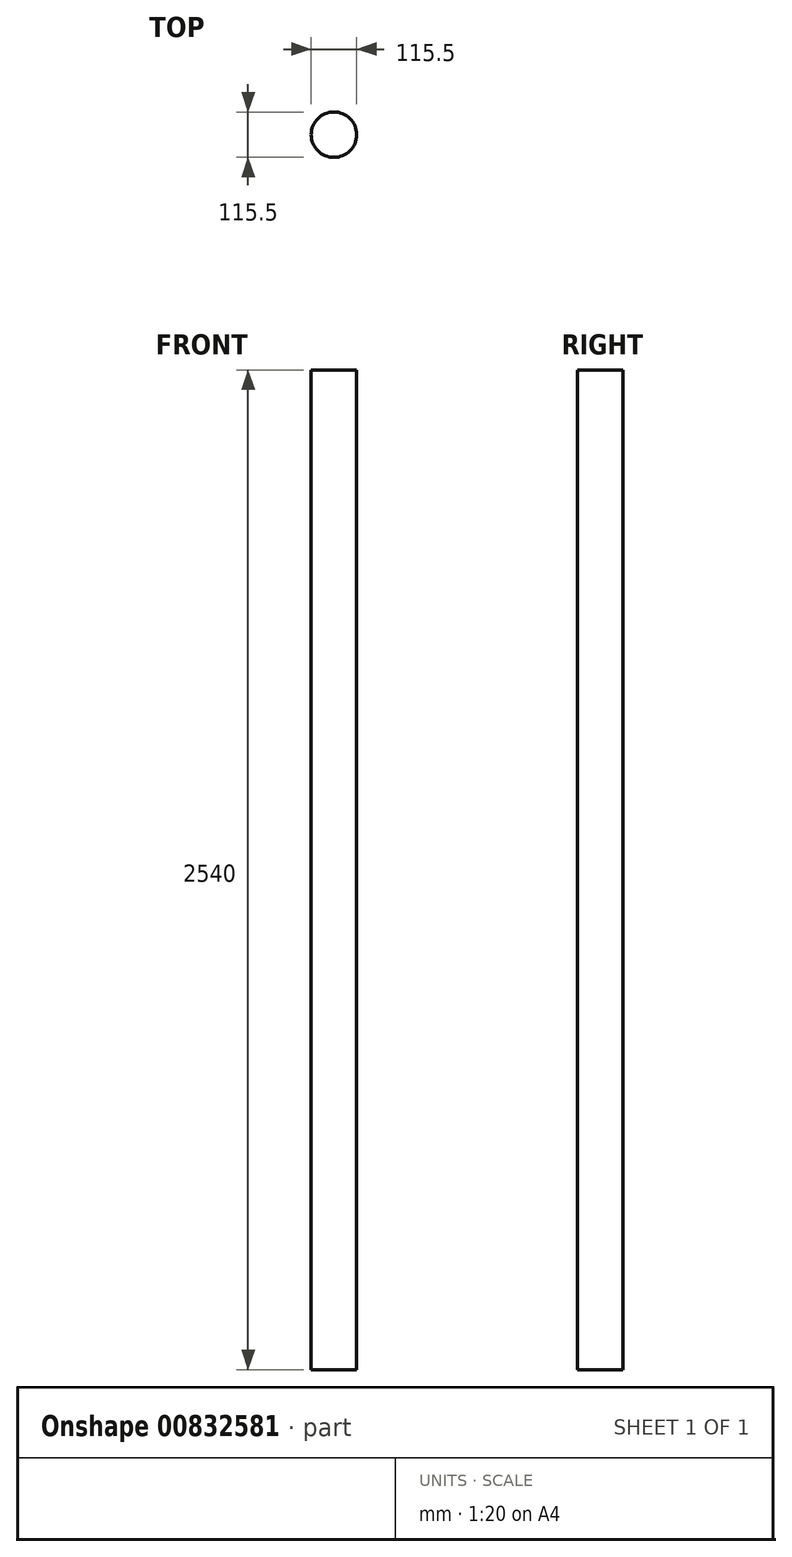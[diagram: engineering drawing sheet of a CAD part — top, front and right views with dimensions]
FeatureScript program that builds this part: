
annotation { "Feature Type Name" : "Feature", "Feature Type Description" : "" }
export const myFeature = defineFeature(function(context is Context, id is Id, definition is map)
    precondition{}
    {
        {
            var Q0;
            Q0=qCreatedBy(makeId("Top.planeOp"),FACE);
            var sketch = newSketch(context, id + "F0", { "sketchPlane" : qUnion([Q0])});
            skCircle(sketch, "E0", {"center": v(0, 0) * mm, "radius": 57.75 * mm});
            skSolve(sketch);
        }
        {
            var Q0;
            Q0 = qSketchRegion(id + "F0", true);
            extrude(context, id + "F1", {"entities" : qUnion([Q0]), "depth" : 2540 * mm, "offsetDistance" : 25.4 * mm});
        }
    });
